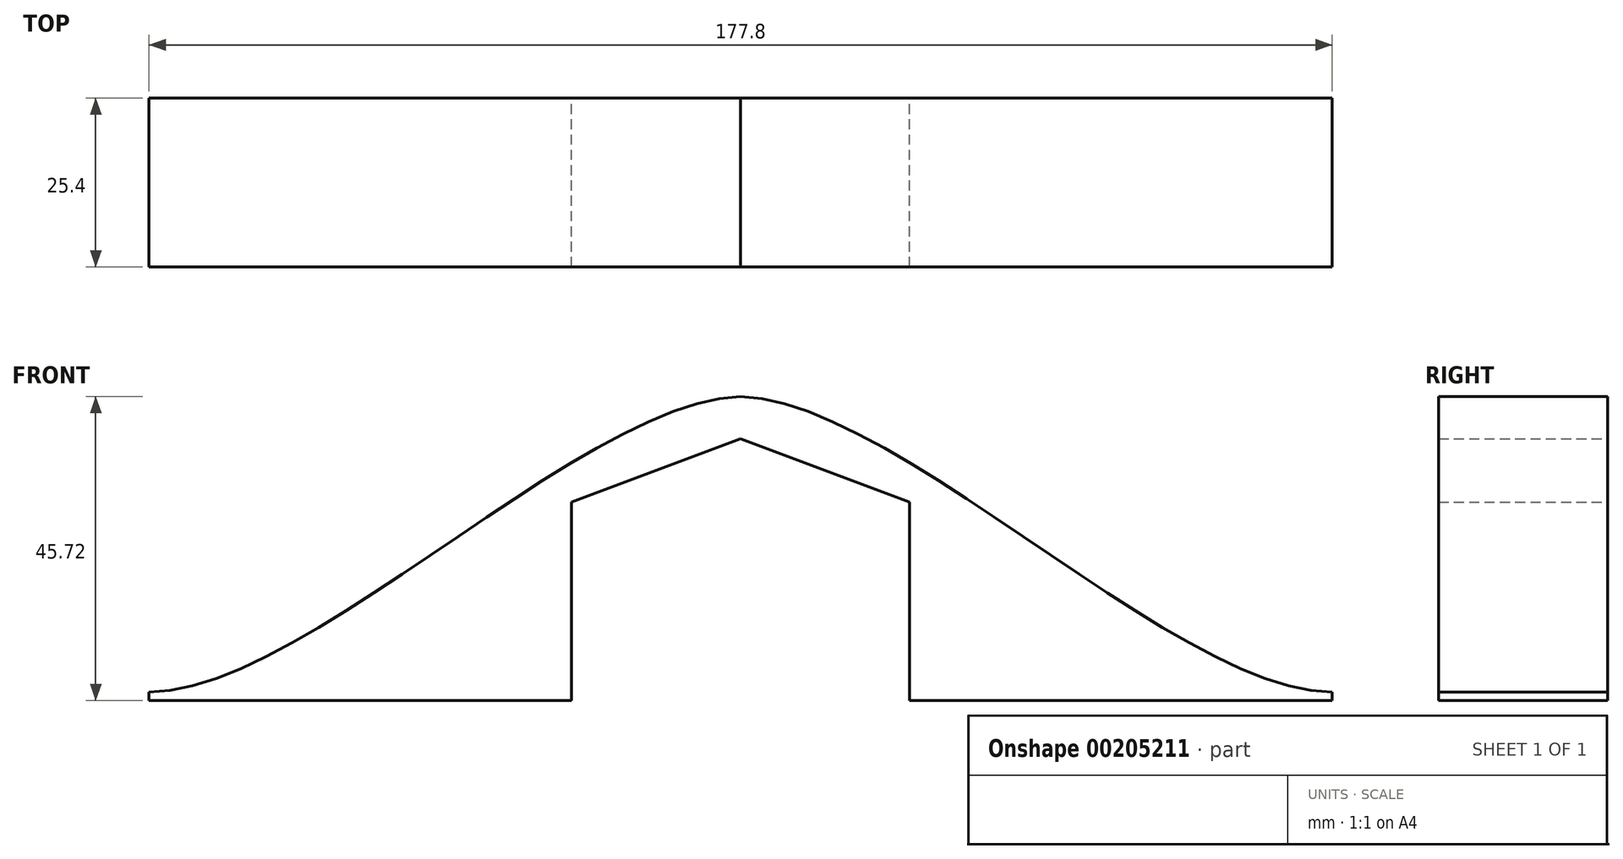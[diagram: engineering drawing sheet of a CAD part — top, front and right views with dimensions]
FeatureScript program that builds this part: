
annotation { "Feature Type Name" : "Feature", "Feature Type Description" : "" }
export const myFeature = defineFeature(function(context is Context, id is Id, definition is map)
    precondition{}
    {
        {
            var Q0;
            Q0=qCreatedBy(makeId("Front.planeOp"),FACE);
            var sketch = newSketch(context, id + "F0", { "sketchPlane" : qUnion([Q0])});
            skLineSegment(sketch, "E0", {"start": v(25.4, 0) * mm, "end": v(88.9, 0) * mm});
            skLineSegment(sketch, "E1", {"start": v(0, 0) * mm, "end": v(0, 38.1) * mm, "construction": true});
            skFitSpline(sketch, "E2", {"points": [v(0, 44.45) * mm, v(88.9, 0) * mm], "startDerivative": vector(71.4, -1.75) * mm, "endDerivative": vector(70.77, 0) * mm});
            skLineSegment(sketch, "E3", {"start": v(0, 38.1) * mm, "end": v(0, 44.45) * mm});
            skLineSegment(sketch, "E4", {"start": v(25.4, 0) * mm, "end": v(25.4, 28.58) * mm});
            skLineSegment(sketch, "E5", {"start": v(25.4, 28.57) * mm, "end": v(0, 38.1) * mm});
            skSolve(sketch);
        }
        {
            var Q0;
            Q0 = qSketchRegion(id + "F0", true);
            extrude(context, id + "F1", {"entities" : qUnion([Q0]), "depth" : 25.4 * mm, "symmetric" : true});
        }
        {
            var Q0;
            Q0=makeQuery(id+"F1.opExtrude","SWEPT_FACE",FACE,{"disambiguationData":[OSD([sQuery(id+"F0.wireOp",EDGE,"E0")])]});
            var sketch = newSketch(context, id + "F2", { "sketchPlane" : qUnion([Q0])});
            skLineSegment(sketch, "E6.0.0", {"start": v(25.4, -12.7) * mm, "end": v(88.9, -12.7) * mm});
            skLineSegment(sketch, "E6.0.1", {"start": v(88.9, -12.7) * mm, "end": v(88.9, 12.7) * mm});
            skLineSegment(sketch, "E6.0.2", {"start": v(88.9, 12.7) * mm, "end": v(25.4, 12.7) * mm});
            skLineSegment(sketch, "E6.0.3", {"start": v(25.4, 12.7) * mm, "end": v(25.4, -12.7) * mm});
            skSolve(sketch);
        }
        {
            var Q0;
            Q0 = qSketchRegion(id + "F2", true);
            extrude(context, id + "F3", {"entities" : qUnion([Q0]), "operationType" : NewBodyOperationType.ADD, "depth" : 1.27 * mm});
        }
        {
            var Q0;
            Q0=makeQuery(id+"F1.opExtrude","SWEPT_BODY",BODY,{"disambiguationData":[OSD([sQuery(id+"F0.wireOp",EDGE,"E0"),sQuery(id+"F0.wireOp",EDGE,"E2"),sQuery(id+"F0.wireOp",EDGE,"E3"),sQuery(id+"F0.wireOp",EDGE,"E4"),sQuery(id+"F0.wireOp",EDGE,"E5")])]});
            var Q1;
            Q1=makeQuery(id+"F1.opExtrude","SWEPT_FACE",FACE,{"disambiguationData":[OSD([sQuery(id+"F0.wireOp",EDGE,"E3")])]});
            mirror(context, id + "F4", {"operationType" : NewBodyOperationType.ADD, "entities" : qUnion([Q0]), "mirrorPlane" : qUnion([Q1])});
        }
    });
